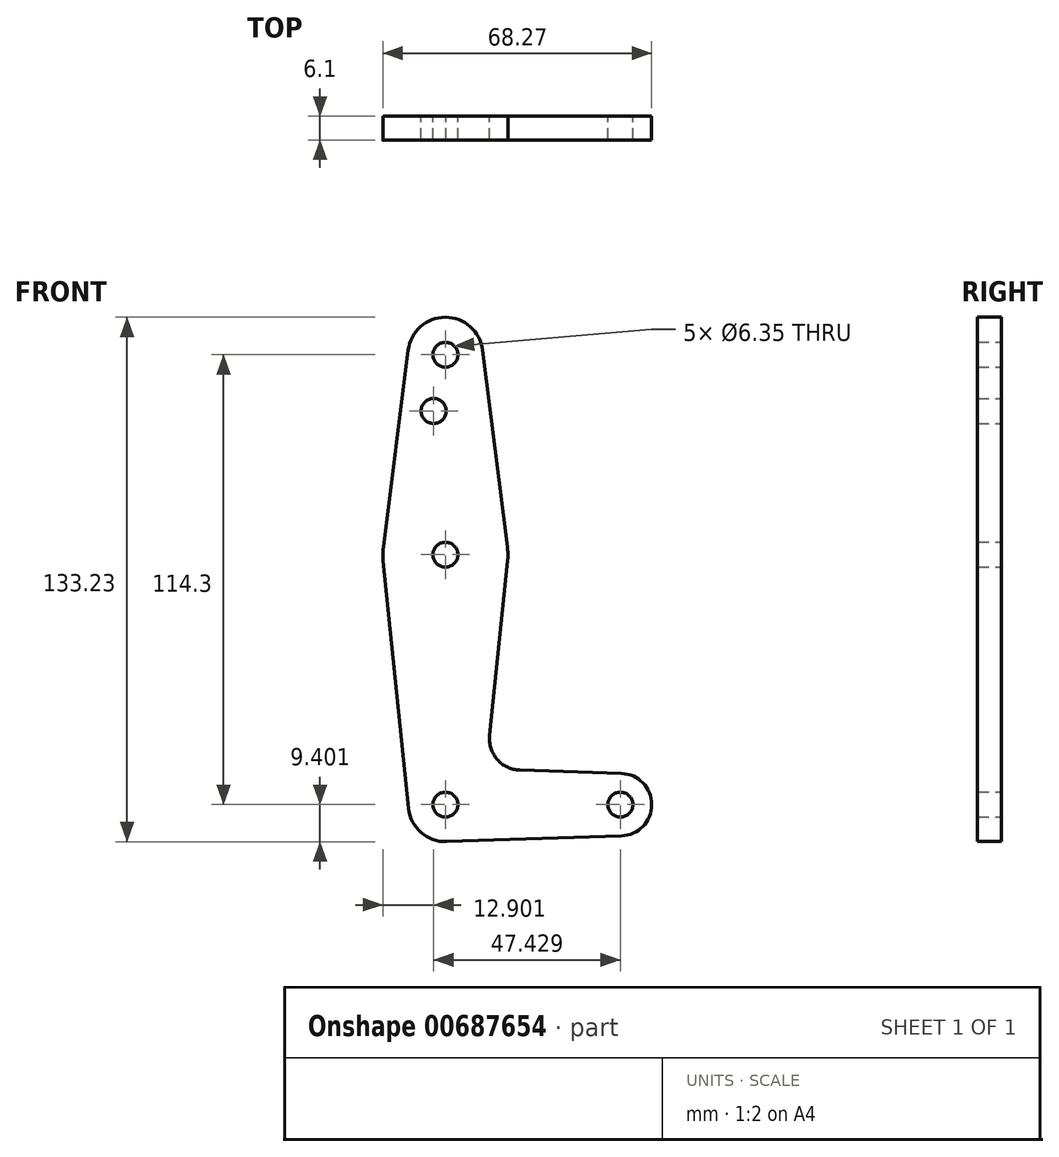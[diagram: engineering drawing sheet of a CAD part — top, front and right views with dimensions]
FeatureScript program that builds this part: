
annotation { "Feature Type Name" : "Feature", "Feature Type Description" : "" }
export const myFeature = defineFeature(function(context is Context, id is Id, definition is map)
    precondition{}
    {
        {
            var Q0;
            Q0=qCreatedBy(makeId("Front.planeOp"),FACE);
            var sketch = newSketch(context, id + "F0", { "sketchPlane" : qUnion([Q0])});
            skLineSegment(sketch, "E0", {"start": v(-44.45, 84.31) * mm, "end": v(-44.45, -29.99) * mm, "construction": true});
            skLineSegment(sketch, "E1", {"start": v(-44.45, -29.99) * mm, "end": v(0, -29.99) * mm, "construction": true});
            skCircle(sketch, "E2", {"center": v(-44.45, 84.31) * mm, "radius": 9.53 * mm});
            skCircle(sketch, "E3", {"center": v(-44.45, 33.51) * mm, "radius": 15.88 * mm});
            skCircle(sketch, "E4", {"center": v(-44.45, -29.99) * mm, "radius": 9.4 * mm});
            skCircle(sketch, "E5", {"center": v(0, -29.99) * mm, "radius": 7.94 * mm});
            skLineSegment(sketch, "E6", {"start": v(-35, 85.5) * mm, "end": v(-28.7, 35.5) * mm});
            skLineSegment(sketch, "E7", {"start": v(-53.9, 85.5) * mm, "end": v(-60.2, 35.5) * mm});
            skLineSegment(sketch, "E8", {"start": v(-60.24, 31.9) * mm, "end": v(-53.8, -30.95) * mm});
            skLineSegment(sketch, "E9", {"start": v(-25.56, -21.2) * mm, "end": v(0.26, -22.06) * mm});
            skLineSegment(sketch, "E10", {"start": v(-28.66, 31.9) * mm, "end": v(-33.2, -12.45) * mm});
            skLineSegment(sketch, "E11", {"start": v(-44.14, -39.38) * mm, "end": v(0.26, -37.92) * mm});
            skCircle(sketch, "E12", {"center": v(-44.45, 84.31) * mm, "radius": 3.18 * mm});
            skCircle(sketch, "E13", {"center": v(-47.43, 70.04) * mm, "radius": 3.18 * mm});
            skCircle(sketch, "E14", {"center": v(-44.45, 33.51) * mm, "radius": 3.18 * mm});
            skCircle(sketch, "E15", {"center": v(-44.45, -29.99) * mm, "radius": 3.18 * mm});
            skCircle(sketch, "E16", {"center": v(0, -29.99) * mm, "radius": 3.18 * mm});
            skArc(sketch, "E17.filletArc", {"start": v(-33.2, -12.45) * mm, "mid": v(-31.28, -18.5) * mm, "end": v(-25.56, -21.2) * mm});
            skSolve(sketch);
        }
        {
            var Q0;
            Q0 = qSketchRegion(id + "F0", true);
            extrude(context, id + "F1", {"entities" : qUnion([Q0]), "depth" : 3.05 * mm, "offsetDistance" : 25.4 * mm});
        }
        {
            var Q0;
            Q0=makeQuery(id+"F1.opExtrude","CAP_FACE",FACE,{"disambiguationData":[OSD([sQuery(id+"F0.wireOp",EDGE,"E2"),sQuery(id+"F0.wireOp",EDGE,"E3"),sQuery(id+"F0.wireOp",EDGE,"E4"),sQuery(id+"F0.wireOp",EDGE,"E5"),sQuery(id+"F0.wireOp",EDGE,"E6"),sQuery(id+"F0.wireOp",EDGE,"E7"),sQuery(id+"F0.wireOp",EDGE,"E8"),sQuery(id+"F0.wireOp",EDGE,"E9"),sQuery(id+"F0.wireOp",EDGE,"E10"),sQuery(id+"F0.wireOp",EDGE,"E11"),sQuery(id+"F0.wireOp",EDGE,"E12"),sQuery(id+"F0.wireOp",EDGE,"E13"),sQuery(id+"F0.wireOp",EDGE,"E14"),sQuery(id+"F0.wireOp",EDGE,"E15"),sQuery(id+"F0.wireOp",EDGE,"E16"),sQuery(id+"F0.wireOp",EDGE,"E17.filletArc")])],"isStart":false});
            extrude(context, id + "F2", {"entities" : qUnion([Q0]), "operationType" : NewBodyOperationType.ADD, "depth" : 3.05 * mm, "offsetDistance" : 25.4 * mm});
        }
    });
